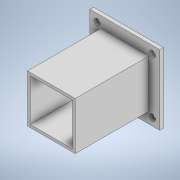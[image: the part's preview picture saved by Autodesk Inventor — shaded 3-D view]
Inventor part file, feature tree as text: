
AUTODESK INVENTOR PART (.ipt)
format: ipt  version: 2022.2 (Build 262287030, 287C)  size: 134,144 bytes
history: native  units: in
note: dims shown in document units (in); Inventor stores cm internally (conversion verified against a paired STEP export)
features: sketch x3, extrude x2, hole x1, projected_geometry x1
ambient origin geometry x8: Origin, YZ Plane, XZ Plane, XY Plane, X Axis, Y Axis, Z Axis, Center Point
bodies: Solid1 (feature_tree)
feature tree (7):
  extrude  "Extrusion1"  Depth=1.4961in
  extrude  "Extrusion2"  Depth=0.8661in
  hole  "Hole1"  [1 undecoded]
  sketch  "Sketch1"  dims[d0=1.4961in d1=1.4961in]
  sketch  "Sketch2"  dims[d2=0.8661in d3=0.8661in]
  sketch  "Sketch3"  dims[d4=0.0787in d5=0.0in d6=1.0236in d7=1.0236in d8=0.9055in d9=1.5748in d10=0.0in d11=0.5906in d12=0.5906in d13=0.7874in d15=1.1811in d16=0.7874in d18=1.1811in d21=0.1339in d22=0.2362in d23=0.1476in d24=0.0984in d25=90.0deg d26=0.3937in d27=0.8108in]
  projected_geometry  "Project Cut Edges1"
note: 1 required parameter value undecoded (feature->parameter linkage not recoverable at this tier; creation-order binding heuristic only, values carry confidence <= 0.55)
